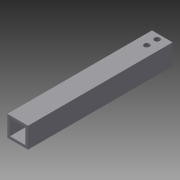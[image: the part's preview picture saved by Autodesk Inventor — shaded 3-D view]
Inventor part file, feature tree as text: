
AUTODESK INVENTOR PART (.ipt)
format: ipt  version: 2013 (Build 170138000, 138)  size: 97,280 bytes
history: native  units: in
note: dims shown in document units (in); Inventor stores cm internally (conversion verified against a paired STEP export)
features: extrude x2, sketch x2, reference x2
ambient origin geometry x8: Origin, YZ Plane, XZ Plane, XY Plane, X Axis, Y Axis, Z Axis, Center Point
bodies: Solid1 (feature_tree)
feature tree (6):
  extrude  "Extrusion1"  Depth=1.0in
  extrude  "Extrusion2"  Depth=7.0in TaperAngle=0.0deg
  sketch  "Sketch1"  dims[d0=1.0in d2=1.0in]
  sketch  "Sketch2"  dims[d3=0.125in d4=7.0in d5=0.0in d6=1.0in d7=0.0in]
  reference  "Reference1"
  reference  "Reference2"
